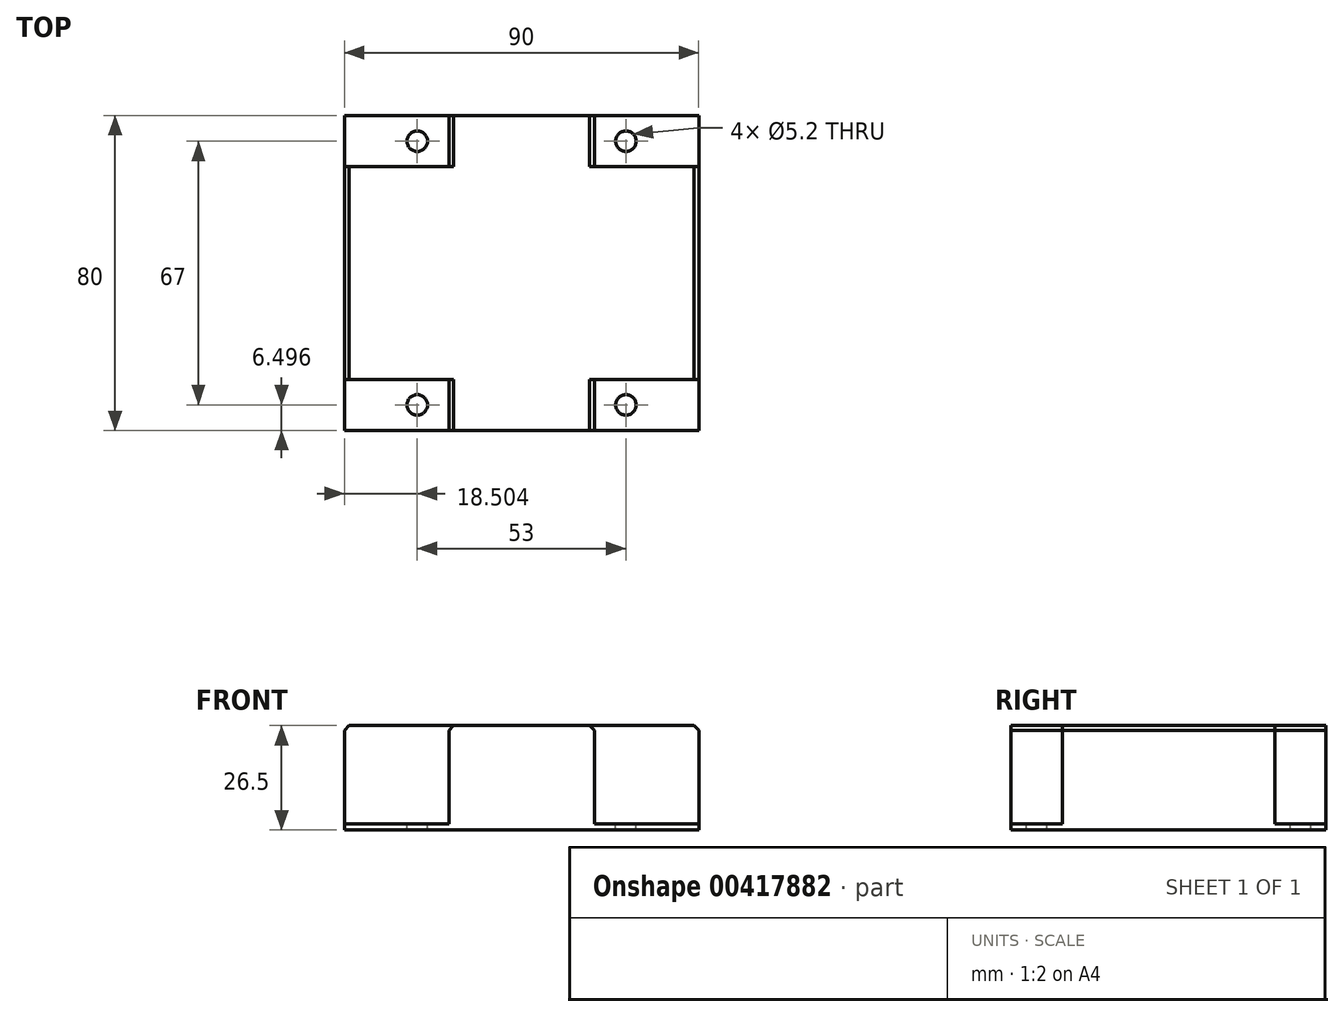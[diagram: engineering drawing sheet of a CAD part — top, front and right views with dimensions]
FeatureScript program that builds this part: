
annotation { "Feature Type Name" : "Feature", "Feature Type Description" : "" }
export const myFeature = defineFeature(function(context is Context, id is Id, definition is map)
    precondition{}
    {
        {
            var Q0;
            Q0=qCreatedBy(makeId("Top.planeOp"),FACE);
            var sketch = newSketch(context, id + "F0", { "sketchPlane" : qUnion([Q0])});
            skLineSegment(sketch, "E0.bottom", {"start": v(-40.48, 31.9) * mm, "end": v(49.52, 31.9) * mm});
            skLineSegment(sketch, "E0.top", {"start": v(-40.48, -48.1) * mm, "end": v(49.52, -48.1) * mm});
            skLineSegment(sketch, "E0.left", {"start": v(-40.48, 31.9) * mm, "end": v(-40.48, -48.1) * mm});
            skLineSegment(sketch, "E0.right", {"start": v(49.52, 31.9) * mm, "end": v(49.52, -48.1) * mm});
            skSolve(sketch);
        }
        {
            var Q0;
            Q0 = qSketchRegion(id + "F0", true);
            extrude(context, id + "F1", {"entities" : qUnion([Q0]), "depth" : 1.5 * mm});
        }
        {
            var Q0;
            Q0=makeQuery(id+"F1.opExtrude","CAP_FACE",FACE,{"disambiguationData":[OSD([sQuery(id+"F0.wireOp",EDGE,"E0.bottom"),sQuery(id+"F0.wireOp",EDGE,"E0.top"),sQuery(id+"F0.wireOp",EDGE,"E0.left"),sQuery(id+"F0.wireOp",EDGE,"E0.right")])],"isStart":false});
            var sketch = newSketch(context, id + "F2", { "sketchPlane" : qUnion([Q0])});
            skLineSegment(sketch, "E1.bottom", {"start": v(-40.48, 31.9) * mm, "end": v(-13.98, 31.9) * mm});
            skLineSegment(sketch, "E1.top", {"start": v(-40.48, 18.9) * mm, "end": v(-13.98, 18.9) * mm});
            skLineSegment(sketch, "E1.left", {"start": v(-40.48, 31.9) * mm, "end": v(-40.48, 18.9) * mm});
            skLineSegment(sketch, "E1.right", {"start": v(-13.98, 31.9) * mm, "end": v(-13.98, 18.9) * mm});
            skLineSegment(sketch, "E2.bottom", {"start": v(-40.48, -35.1) * mm, "end": v(-13.98, -35.1) * mm});
            skLineSegment(sketch, "E2.top", {"start": v(-40.48, -48.1) * mm, "end": v(-13.98, -48.1) * mm});
            skLineSegment(sketch, "E2.left", {"start": v(-40.48, -35.1) * mm, "end": v(-40.48, -48.1) * mm});
            skLineSegment(sketch, "E2.right", {"start": v(-13.98, -35.1) * mm, "end": v(-13.98, -48.1) * mm});
            skLineSegment(sketch, "E3.bottom", {"start": v(23.02, -35.1) * mm, "end": v(49.52, -35.1) * mm});
            skLineSegment(sketch, "E3.top", {"start": v(23.02, -48.1) * mm, "end": v(49.52, -48.1) * mm});
            skLineSegment(sketch, "E3.left", {"start": v(23.02, -35.1) * mm, "end": v(23.02, -48.1) * mm});
            skLineSegment(sketch, "E3.right", {"start": v(49.52, -35.1) * mm, "end": v(49.52, -48.1) * mm});
            skLineSegment(sketch, "E4.bottom", {"start": v(23.02, 31.9) * mm, "end": v(49.52, 31.9) * mm});
            skLineSegment(sketch, "E4.top", {"start": v(23.02, 18.9) * mm, "end": v(49.52, 18.9) * mm});
            skLineSegment(sketch, "E4.left", {"start": v(23.02, 31.9) * mm, "end": v(23.02, 18.9) * mm});
            skLineSegment(sketch, "E4.right", {"start": v(49.52, 31.9) * mm, "end": v(49.52, 18.9) * mm});
            skPoint(sketch, "E5", {"position": v(-21.98, 25.4) * mm});
            skLineSegment(sketch, "E6", {"start": v(0, 31.9) * mm, "end": v(0, -35.5) * mm});
            skLineSegment(sketch, "E7", {"start": v(-35.34, 0) * mm, "end": v(33.43, 0) * mm});
            skPoint(sketch, "E8", {"position": v(31.02, 25.4) * mm});
            skPoint(sketch, "E9", {"position": v(-21.98, -41.6) * mm});
            skPoint(sketch, "E10", {"position": v(31.02, -41.6) * mm});
            skSolve(sketch);
        }
        {
            var Q0;
            {var subQ8=sQuery(id+"F2.wireOp",EDGE,"E1.top");Q0=makeQuery(id+"F2.imprint","IMPRINT",FACE,{"disambiguationData":[TD([[makeQuery(id+"F2.imprint","IMPRINT",EDGE,{"derivedFrom":subQ8}),-1.0]])]});}
            extrude(context, id + "F3", {"entities" : qUnion([Q0]), "operationType" : NewBodyOperationType.ADD, "depth" : 25 * mm});
        }
        {
            var Q0;
            Q0=sQuery(id+"F2.wireOp",VERTEX,"E5");
            var Q1;
            Q1=sQuery(id+"F2.wireOp",VERTEX,"E8");
            var Q2;
            Q2=sQuery(id+"F2.wireOp",VERTEX,"E10");
            var Q3;
            Q3=sQuery(id+"F2.wireOp",VERTEX,"E9");
            var Q4;
            Q4=makeQuery(id+"F1.opExtrude","SWEPT_BODY",BODY,{"disambiguationData":[OSD([sQuery(id+"F0.wireOp",EDGE,"E0.bottom"),sQuery(id+"F0.wireOp",EDGE,"E0.top"),sQuery(id+"F0.wireOp",EDGE,"E0.left"),sQuery(id+"F0.wireOp",EDGE,"E0.right")])]});
            hole(context, id + "F4", {"style" : HoleStyle.SIMPLE, "endStyle" : HoleEndStyle.BLIND, "holeDiameter" : 5.2 * mm, "holeDepth" : 5 * mm, "isTappedThrough" : true, "tappedDepth" : 12 * mm, "tapClearance" : 3, "locations" : qUnion([Q0, Q1, Q2, Q3]), "scope" : qUnion([Q4])});
        }
        {
            var Q0;
            Q0=makeQuery(id+"F3.opExtrude","CAP_EDGE",EDGE,{"disambiguationData":[OSD([sQuery(id+"F0.wireOp",EDGE,"E0.left")])],"isStart":false});
            var Q1;
            Q1=makeQuery(id+"F3.opExtrude","CAP_EDGE",EDGE,{"disambiguationData":[OSD([sQuery(id+"F2.wireOp",EDGE,"E2.right")])],"isStart":false});
            var Q2;
            Q2=makeQuery(id+"F3.opExtrude","CAP_EDGE",EDGE,{"disambiguationData":[OSD([sQuery(id+"F2.wireOp",EDGE,"E1.right")])],"isStart":false});
            var Q3;
            Q3=makeQuery(id+"F3.opExtrude","CAP_EDGE",EDGE,{"disambiguationData":[OSD([sQuery(id+"F2.wireOp",EDGE,"E4.left")])],"isStart":false});
            var Q4;
            Q4=makeQuery(id+"F3.opExtrude","CAP_EDGE",EDGE,{"disambiguationData":[OSD([sQuery(id+"F2.wireOp",EDGE,"E3.left")])],"isStart":false});
            var Q5;
            Q5=makeQuery(id+"F3.opExtrude","CAP_EDGE",EDGE,{"disambiguationData":[OSD([sQuery(id+"F0.wireOp",EDGE,"E0.right")])],"isStart":false});
            chamfer(context, id + "F5", {"entities" : qUnion([Q0, Q1, Q2, Q3, Q4, Q5]), "width" : 1.2 * mm, "tangentPropagation" : true});
        }
    });
